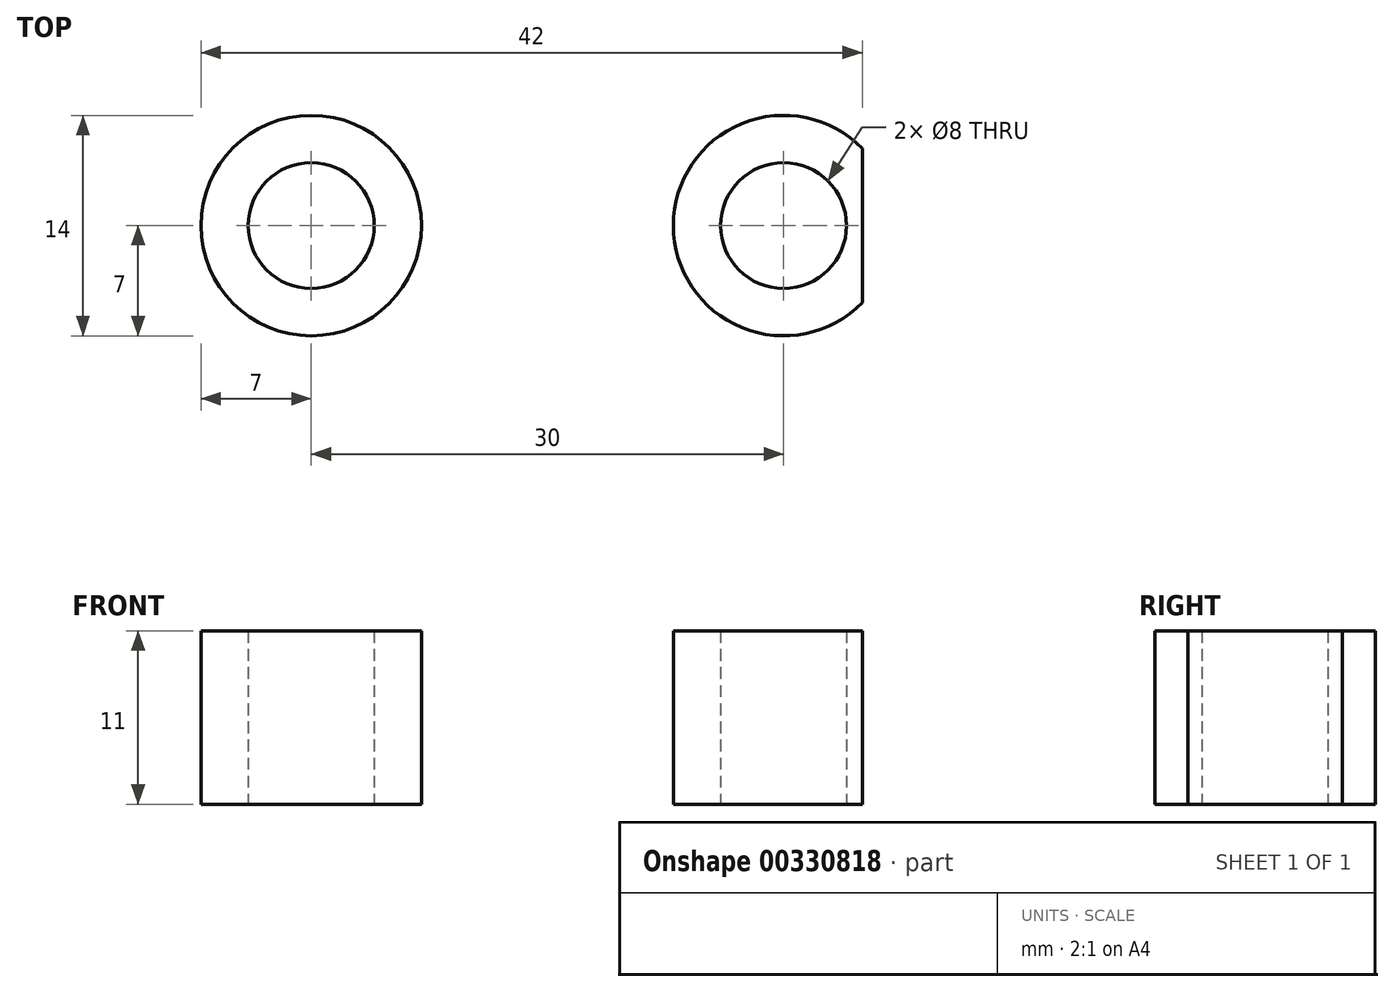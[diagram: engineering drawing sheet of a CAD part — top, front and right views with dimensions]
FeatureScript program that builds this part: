
annotation { "Feature Type Name" : "Feature", "Feature Type Description" : "" }
export const myFeature = defineFeature(function(context is Context, id is Id, definition is map)
    precondition{}
    {
        {
            var Q0;
            Q0=qCreatedBy(makeId("Top.planeOp"),FACE);
            var sketch = newSketch(context, id + "F0", { "sketchPlane" : qUnion([Q0])});
            skCircle(sketch, "E0", {"center": v(-15, 0) * mm, "radius": 7 * mm});
            skCircle(sketch, "E1", {"center": v(-15, 0) * mm, "radius": 4 * mm});
            skCircle(sketch, "E2", {"center": v(15, 0) * mm, "radius": 4 * mm});
            skCircle(sketch, "E3", {"center": v(15, 0) * mm, "radius": 7 * mm});
            skSolve(sketch);
        }
        {
            var Q0;
            Q0 = qSketchRegion(id + "F0", true);
            extrude(context, id + "F1", {"entities" : qUnion([Q0]), "depth" : 11 * mm});
        }
        {
            var Q0;
            Q0=makeQuery(id+"F1.opExtrude","CAP_FACE",FACE,{"disambiguationData":[OSD([sQuery(id+"F0.wireOp",EDGE,"E2"),sQuery(id+"F0.wireOp",EDGE,"E3")])],"isStart":false});
            var sketch = newSketch(context, id + "F2", { "sketchPlane" : qUnion([Q0])});
            skLineSegment(sketch, "E4.bottom", {"start": v(25.95, 10.85) * mm, "end": v(20, 10.85) * mm});
            skLineSegment(sketch, "E4.top", {"start": v(25.95, -12.58) * mm, "end": v(20, -12.58) * mm});
            skLineSegment(sketch, "E4.left", {"start": v(25.95, 10.85) * mm, "end": v(25.95, -12.58) * mm});
            skLineSegment(sketch, "E4.right", {"start": v(20, 10.85) * mm, "end": v(20, -12.58) * mm});
            skSolve(sketch);
        }
        {
            var Q0;
            Q0 = qSketchRegion(id + "F2", true);
            extrude(context, id + "F3", {"entities" : qUnion([Q0]), "operationType" : NewBodyOperationType.REMOVE, "endBound" : BoundingType.THROUGH_ALL, "oppositeDirection" : true, "depth" : 25 * mm});
        }
    });
